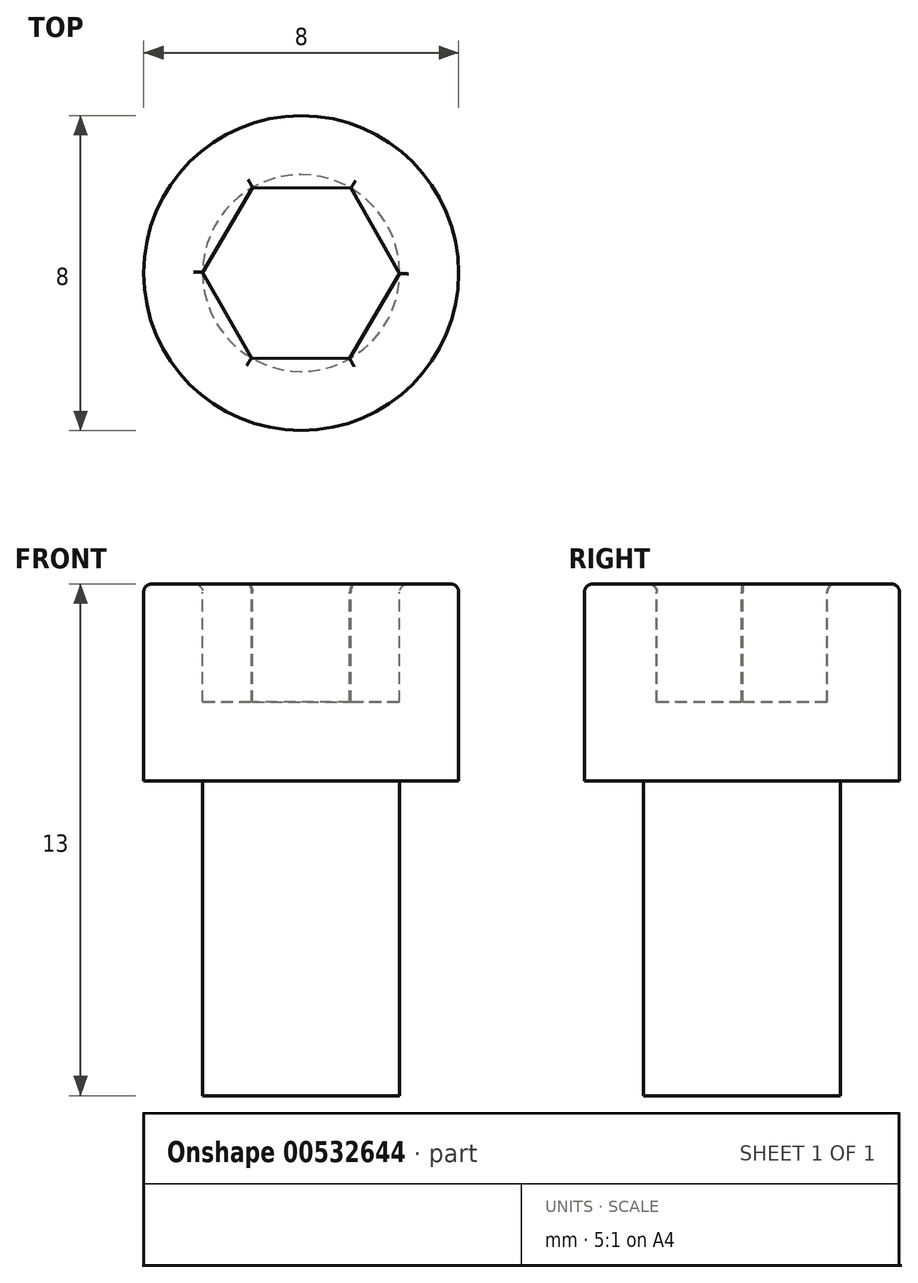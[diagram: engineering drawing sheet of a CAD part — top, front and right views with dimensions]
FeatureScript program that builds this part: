
annotation { "Feature Type Name" : "Feature", "Feature Type Description" : "" }
export const myFeature = defineFeature(function(context is Context, id is Id, definition is map)
    precondition{}
    {
        {
            var Q0;
            Q0=qCreatedBy(makeId("Top.planeOp"),FACE);
            var sketch = newSketch(context, id + "F0", { "sketchPlane" : qUnion([Q0])});
            skCircle(sketch, "E0", {"center": v(0, 0) * mm, "radius": 4 * mm});
            skSolve(sketch);
        }
        {
            var Q0;
            Q0=makeQuery(id+"F0.imprint","IMPRINT",FACE,{"disambiguationData":[TD([[makeQuery(id+"F0.imprint","IMPRINT",EDGE,{"derivedFrom":sQuery(id+"F0.wireOp",EDGE,"E0")}),1.0]])]});
            var sketch = newSketch(context, id + "F1", { "sketchPlane" : qUnion([Q0])});
            skCircle(sketch, "E1", {"center": v(0, 0) * mm, "radius": 2.5 * mm});
            skSolve(sketch);
        }
        {
            var Q0;
            Q0=makeQuery(id+"F1.imprint","IMPRINT",FACE,{"disambiguationData":[TD([[makeQuery(id+"F1.imprint","IMPRINT",EDGE,{"derivedFrom":sQuery(id+"F1.wireOp",EDGE,"E1")}),1.0]])]});
            extrude(context, id + "F2", {"entities" : qUnion([Q0]), "oppositeDirection" : true, "depth" : 13 * mm, "offsetDistance" : 25 * mm});
        }
        {
            var Q0;
            Q0=makeQuery(id+"F0.imprint","IMPRINT",FACE,{"disambiguationData":[TD([[makeQuery(id+"F0.imprint","IMPRINT",EDGE,{"derivedFrom":sQuery(id+"F0.wireOp",EDGE,"E0")}),1.0]])]});
            extrude(context, id + "F3", {"entities" : qUnion([Q0]), "operationType" : NewBodyOperationType.ADD, "oppositeDirection" : true, "depth" : 5 * mm, "offsetDistance" : 25 * mm});
        }
        {
            var Q0;
            Q0=qCreatedBy(makeId("Top.planeOp"),FACE);
            var sketch = newSketch(context, id + "F4", { "sketchPlane" : qUnion([Q0])});
            skCircle(sketch, "E2.cCircle", {"center": v(0, 0) * mm, "radius": 2.5 * mm, "construction": true});
            skLineSegment(sketch, "E2.0", {"start": v(1.27, 2.16) * mm, "end": v(2.5, -0.02) * mm});
            skLineSegment(sketch, "E2.1", {"start": v(2.5, -0.02) * mm, "end": v(1.23, -2.17) * mm});
            skLineSegment(sketch, "E2.2", {"start": v(1.23, -2.17) * mm, "end": v(-1.27, -2.16) * mm});
            skLineSegment(sketch, "E2.3", {"start": v(-1.27, -2.16) * mm, "end": v(-2.5, 0.02) * mm});
            skLineSegment(sketch, "E2.4", {"start": v(-2.5, 0.02) * mm, "end": v(-1.23, 2.17) * mm});
            skLineSegment(sketch, "E2.5", {"start": v(-1.23, 2.17) * mm, "end": v(1.27, 2.16) * mm});
            skSolve(sketch);
        }
        {
            var Q0;
            Q0=makeQuery(id+"F4.imprint","IMPRINT",FACE,{"disambiguationData":[TD([[makeQuery(id+"F4.imprint","IMPRINT",EDGE,{"derivedFrom":sQuery(id+"F4.wireOp",EDGE,"E2.0")}),-1.0]])]});
            extrude(context, id + "F5", {"entities" : qUnion([Q0]), "operationType" : NewBodyOperationType.REMOVE, "oppositeDirection" : true, "depth" : 3 * mm, "offsetDistance" : 25 * mm});
        }
        {
            var Q0;
            Q0=makeQuery(id+"F5.boolean.opBoolean","COPY",EDGE,{"derivedFrom":makeQuery(id+"F5.opExtrude","CAP_EDGE",EDGE,{"disambiguationData":[OSD([sQuery(id+"F4.wireOp",EDGE,"E2.1")])],"isStart":true})});
            var Q1;
            Q1=makeQuery(id+"F3.boolean.opBoolean","MERGE",FACE,{"derivedFrom":[makeQuery(id+"F2.opExtrude","CAP_FACE",FACE,{"disambiguationData":[OSD([sQuery(id+"F1.wireOp",EDGE,"E1")])],"isStart":true}),makeQuery(id+"F3.opExtrude","CAP_FACE",FACE,{"disambiguationData":[OSD([sQuery(id+"F0.wireOp",EDGE,"E0")])],"isStart":true})]});
            fillet(context, id + "F6", {"entities" : qUnion([Q0, Q1]), "radius" : 0.2 * mm, "tangentPropagation" : true, "allowEdgeOverflow" : false});
        }
    });
